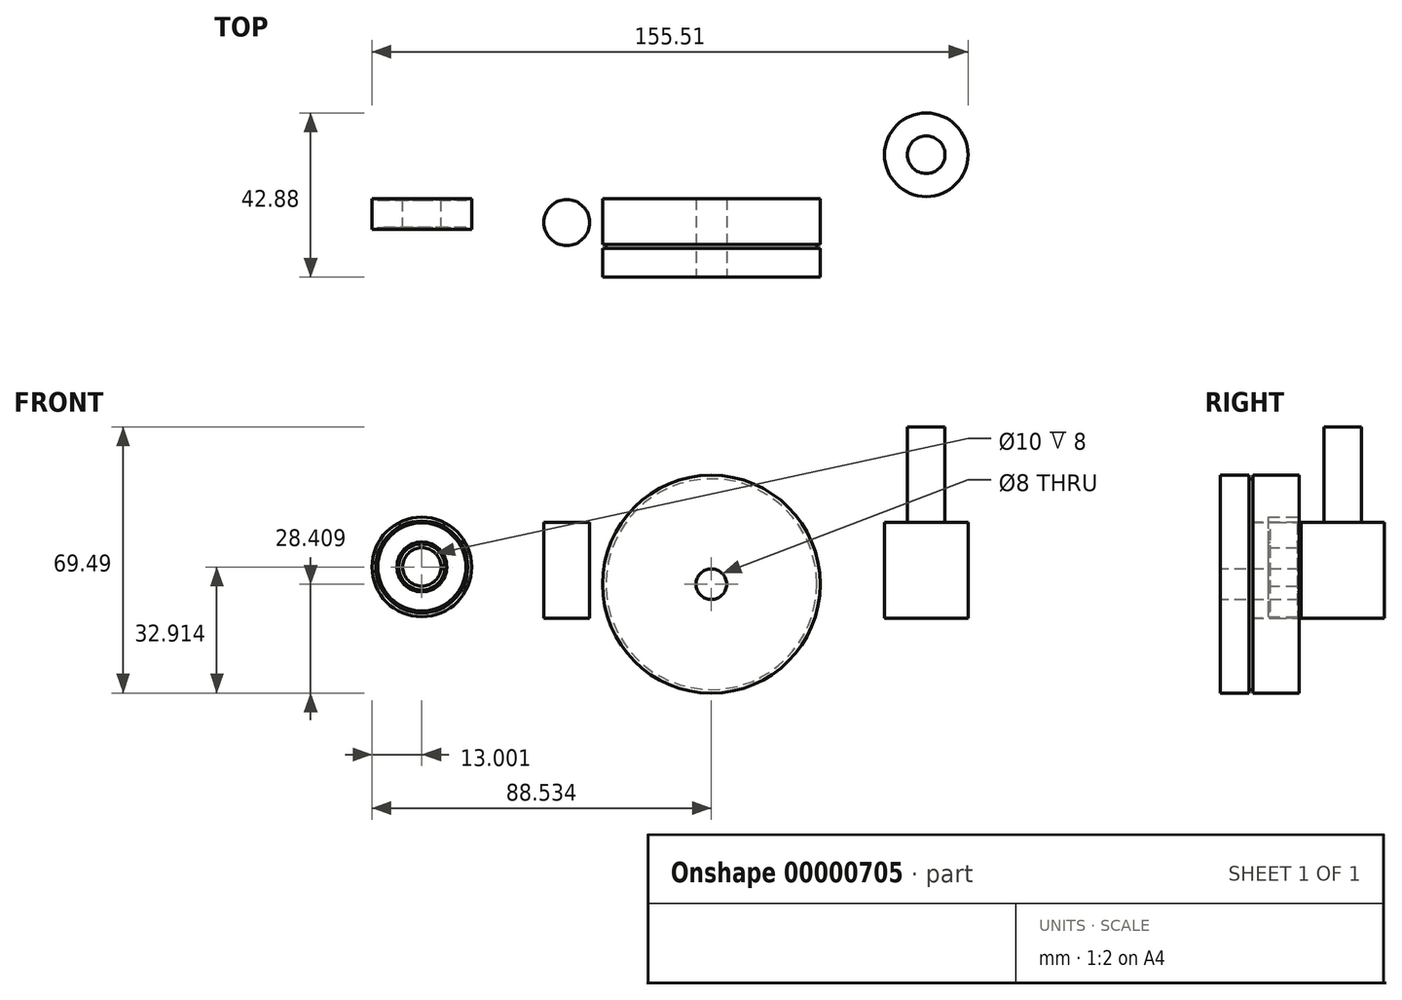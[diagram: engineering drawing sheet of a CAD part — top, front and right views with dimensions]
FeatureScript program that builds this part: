
annotation { "Feature Type Name" : "Feature", "Feature Type Description" : "" }
export const myFeature = defineFeature(function(context is Context, id is Id, definition is map)
    precondition{}
    {
        {
            var Q0;
            Q0=qCreatedBy(makeId("Front.planeOp"),FACE);
            var sketch = newSketch(context, id + "F0", { "sketchPlane" : qUnion([Q0])});
            skCircle(sketch, "E0", {"center": v(-33.09, 8.92) * mm, "radius": 28.4 * mm});
            skSolve(sketch);
        }
        {
            var Q0;
            Q0 = qSketchRegion(id + "F0", true);
            extrude(context, id + "F1", {"entities" : qUnion([Q0]), "depth" : 20.57 * mm});
        }
        {
            var Q0;
            Q0=qCreatedBy(makeId("Top.planeOp"),FACE);
            var sketch = newSketch(context, id + "F2", { "sketchPlane" : qUnion([Q0])});
            skCircle(sketch, "E1", {"center": v(-70.83, -6.28) * mm, "radius": 6 * mm});
            skSolve(sketch);
        }
        {
            var Q0;
            Q0 = qSketchRegion(id + "F2", true);
            extrude(context, id + "F3", {"entities" : qUnion([Q0]), "depth" : 25 * mm});
        }
        {
            var Q0;
            Q0=qCreatedBy(makeId("Front.planeOp"),FACE);
            var sketch = newSketch(context, id + "F4", { "sketchPlane" : qUnion([Q0])});
            skCircle(sketch, "E2", {"center": v(-108.62, 13.42) * mm, "radius": 5 * mm});
            skCircle(sketch, "E3", {"center": v(-108.62, 13.42) * mm, "radius": 13 * mm});
            skSolve(sketch);
        }
        {
            var Q0;
            Q0 = qSketchRegion(id + "F4", true);
            extrude(context, id + "F5", {"entities" : qUnion([Q0]), "depth" : 8 * mm});
        }
        {
            var Q0;
            Q0=makeQuery(id+"F5.opExtrude","CAP_FACE",FACE,{"disambiguationData":[OSD([sQuery(id+"F4.wireOp",EDGE,"E2"),sQuery(id+"F4.wireOp",EDGE,"E3")])],"isStart":false});
            var sketch = newSketch(context, id + "F6", { "sketchPlane" : qUnion([Q0])});
            skCircle(sketch, "E4", {"center": v(-108.62, 13.42) * mm, "radius": 6 * mm});
            skCircle(sketch, "E5", {"center": v(-108.62, 13.42) * mm, "radius": 12 * mm});
            skSolve(sketch);
        }
        {
            var Q0;
            Q0 = qSketchRegion(id + "F6", true);
            extrude(context, id + "F7", {"entities" : qUnion([Q0]), "operationType" : NewBodyOperationType.REMOVE, "oppositeDirection" : true, "depth" : 0.5 * mm});
        }
        {
            var Q0;
            Q0=makeQuery(id+"F7.boolean.opBoolean","COPY",EDGE,{"derivedFrom":makeQuery(id+"F7.opExtrude","CAP_EDGE",EDGE,{"disambiguationData":[OSD([sQuery(id+"F6.wireOp",EDGE,"E5")])],"isStart":false})});
            var Q1;
            Q1=makeQuery(id+"F7.boolean.opBoolean","COPY",EDGE,{"derivedFrom":makeQuery(id+"F7.opExtrude","CAP_EDGE",EDGE,{"disambiguationData":[OSD([sQuery(id+"F6.wireOp",EDGE,"E4")])],"isStart":false})});
            chamfer(context, id + "F8", {"entities" : qUnion([Q0, Q1]), "width" : 0.5 * mm, "tangentPropagation" : true});
        }
        {
            var Q0;
            Q0=makeQuery(id+"F5.opExtrude","CAP_FACE",FACE,{"disambiguationData":[OSD([sQuery(id+"F4.wireOp",EDGE,"E2"),sQuery(id+"F4.wireOp",EDGE,"E3")])],"isStart":true});
            var sketch = newSketch(context, id + "F9", { "sketchPlane" : qUnion([Q0])});
            skCircle(sketch, "E6", {"center": v(108.62, 13.42) * mm, "radius": 6 * mm});
            skCircle(sketch, "E7", {"center": v(108.62, 13.42) * mm, "radius": 12 * mm});
            skSolve(sketch);
        }
        {
            var Q0;
            Q0 = qSketchRegion(id + "F9", true);
            extrude(context, id + "F10", {"entities" : qUnion([Q0]), "operationType" : NewBodyOperationType.REMOVE, "oppositeDirection" : true, "depth" : 0.5 * mm});
        }
        {
            var Q0;
            Q0=makeQuery(id+"F10.boolean.opBoolean","COPY",EDGE,{"derivedFrom":makeQuery(id+"F10.opExtrude","CAP_EDGE",EDGE,{"disambiguationData":[OSD([sQuery(id+"F9.wireOp",EDGE,"E7")])],"isStart":false})});
            var Q1;
            Q1=makeQuery(id+"F10.boolean.opBoolean","COPY",EDGE,{"derivedFrom":makeQuery(id+"F10.opExtrude","CAP_EDGE",EDGE,{"disambiguationData":[OSD([sQuery(id+"F9.wireOp",EDGE,"E6")])],"isStart":false})});
            chamfer(context, id + "F11", {"entities" : qUnion([Q0, Q1]), "width" : 0.5 * mm, "tangentPropagation" : true});
        }
        {
            var Q0;
            Q0=qCreatedBy(makeId("Top.planeOp"),FACE);
            var sketch = newSketch(context, id + "F12", { "sketchPlane" : qUnion([Q0])});
            skCircle(sketch, "E8", {"center": v(23, 11.4) * mm, "radius": 10.9 * mm});
            skSolve(sketch);
        }
        {
            var Q0;
            Q0 = qSketchRegion(id + "F12", true);
            extrude(context, id + "F13", {"entities" : qUnion([Q0]), "depth" : 25 * mm});
        }
        {
            var Q0;
            Q0=makeQuery(id+"F13.opExtrude","CAP_FACE",FACE,{"disambiguationData":[OSD([sQuery(id+"F12.wireOp",EDGE,"E8")])],"isStart":false});
            var sketch = newSketch(context, id + "F14", { "sketchPlane" : qUnion([Q0])});
            skCircle(sketch, "E9", {"center": v(23, 11.4) * mm, "radius": 4.9 * mm});
            skSolve(sketch);
        }
        {
            var Q0;
            Q0 = qSketchRegion(id + "F14", true);
            extrude(context, id + "F15", {"entities" : qUnion([Q0]), "operationType" : NewBodyOperationType.ADD, "depth" : 25 * mm});
        }
        {
            var Q0;
            Q0=makeQuery(id+"F1.opExtrude","CAP_FACE",FACE,{"disambiguationData":[OSD([sQuery(id+"F0.wireOp",EDGE,"E0")])],"isStart":true});
            cPlane(context, id + "F16", {"entities" : qUnion([Q0]), "cplaneType" : CPlaneType.OFFSET, "offset" : 12 * mm, "oppositeDirection" : true, "width" : 150 * mm, "height" : 150 * mm});
        }
        {
            var Q0;
            Q0=qCreatedBy(id+"F16.planeOp",FACE);
            var sketch = newSketch(context, id + "F17", { "sketchPlane" : qUnion([Q0])});
            skCircle(sketch, "E10", {"center": v(33.09, 8.92) * mm, "radius": 27.5 * mm});
            skCircle(sketch, "E11", {"center": v(33.09, 8.92) * mm, "radius": 30.36 * mm});
            skSolve(sketch);
        }
        {
            var Q0;
            Q0 = qSketchRegion(id + "F17", true);
            extrude(context, id + "F18", {"entities" : qUnion([Q0]), "operationType" : NewBodyOperationType.REMOVE, "oppositeDirection" : true, "depth" : 1 * mm});
        }
        {
            var Q0;
            Q0=makeQuery(id+"F1.opExtrude","CAP_FACE",FACE,{"disambiguationData":[OSD([sQuery(id+"F0.wireOp",EDGE,"E0")])],"isStart":false});
            var sketch = newSketch(context, id + "F19", { "sketchPlane" : qUnion([Q0])});
            skCircle(sketch, "E12", {"center": v(-33.09, 8.92) * mm, "radius": 4 * mm});
            skSolve(sketch);
        }
        {
            var Q0;
            Q0 = qSketchRegion(id + "F19", true);
            extrude(context, id + "F20", {"entities" : qUnion([Q0]), "operationType" : NewBodyOperationType.REMOVE, "oppositeDirection" : true, "depth" : 25 * mm});
        }
    });
